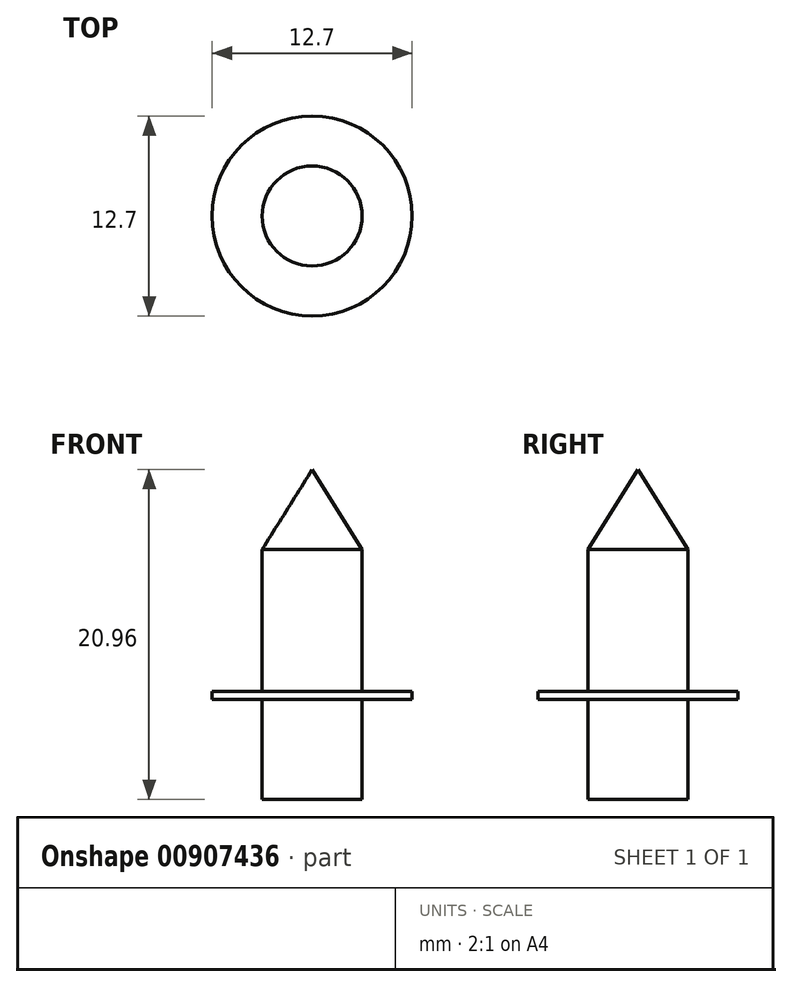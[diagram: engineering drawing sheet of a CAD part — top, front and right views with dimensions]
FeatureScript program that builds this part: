
annotation { "Feature Type Name" : "Feature", "Feature Type Description" : "" }
export const myFeature = defineFeature(function(context is Context, id is Id, definition is map)
    precondition{}
    {
        {
            var Q0;
            Q0=qCreatedBy(makeId("Top.planeOp"),FACE);
            var sketch = newSketch(context, id + "F0", { "sketchPlane" : qUnion([Q0])});
            skCircle(sketch, "E0", {"center": v(0, 0) * mm, "radius": 3.18 * mm});
            skSolve(sketch);
        }
        {
            var Q0;
            Q0 = qSketchRegion(id + "F0", true);
            extrude(context, id + "F1", {"entities" : qUnion([Q0]), "depth" : 15.88 * mm, "offsetDistance" : 25.4 * mm});
        }
        {
            var Q0;
            Q0=qCreatedBy(makeId("Top.planeOp"),FACE);
            cPlane(context, id + "F2", {"entities" : qUnion([Q0]), "cplaneType" : CPlaneType.OFFSET, "offset" : 6.35 * mm, "width" : 152.4 * mm, "height" : 152.4 * mm});
        }
        {
            var Q0;
            Q0=qCreatedBy(id+"F2.planeOp",FACE);
            var sketch = newSketch(context, id + "F3", { "sketchPlane" : qUnion([Q0])});
            skCircle(sketch, "E1", {"center": v(0, 0) * mm, "radius": 6.35 * mm});
            skSolve(sketch);
        }
        {
            var Q0;
            Q0=makeQuery(id+"F3.imprint","IMPRINT",FACE,{"disambiguationData":[TD([[makeQuery(id+"F3.imprint","IMPRINT",EDGE,{"derivedFrom":sQuery(id+"F3.wireOp",EDGE,"E1")}),1.0]])]});
            extrude(context, id + "F4", {"entities" : qUnion([Q0]), "operationType" : NewBodyOperationType.ADD, "depth" : 0.5 * mm, "offsetDistance" : 25.4 * mm});
        }
        {
            var Q0;
            Q0=makeQuery(id+"F1.opExtrude","CAP_FACE",FACE,{"disambiguationData":[OSD([sQuery(id+"F0.wireOp",EDGE,"E0")])],"isStart":false});
            cPlane(context, id + "F5", {"entities" : qUnion([Q0]), "cplaneType" : CPlaneType.OFFSET, "offset" : 5.08 * mm, "width" : 152.4 * mm, "height" : 152.4 * mm});
        }
        {
            var Q0;
            Q0=qCreatedBy(id+"F5.planeOp",FACE);
            var sketch = newSketch(context, id + "F6", { "sketchPlane" : qUnion([Q0])});
            skPoint(sketch, "E2", {"position": v(0, 0) * mm});
            skSolve(sketch);
        }
        {
            var Q1;
            Q1=makeQuery(id+"F1.opExtrude","CAP_FACE",FACE,{"disambiguationData":[OSD([sQuery(id+"F0.wireOp",EDGE,"E0")])],"isStart":false});
            var Q2;
            Q2=sQuery(id+"F6.wireOp",VERTEX,"E2");
            loft(context, id + "F7", {"operationType" : NewBodyOperationType.ADD, "sheetProfilesArray" : [{ "sheetProfileEntities" : qUnion([Q1]) }, { "sheetProfileEntities" : qUnion([Q2]) }]});
        }
    });
